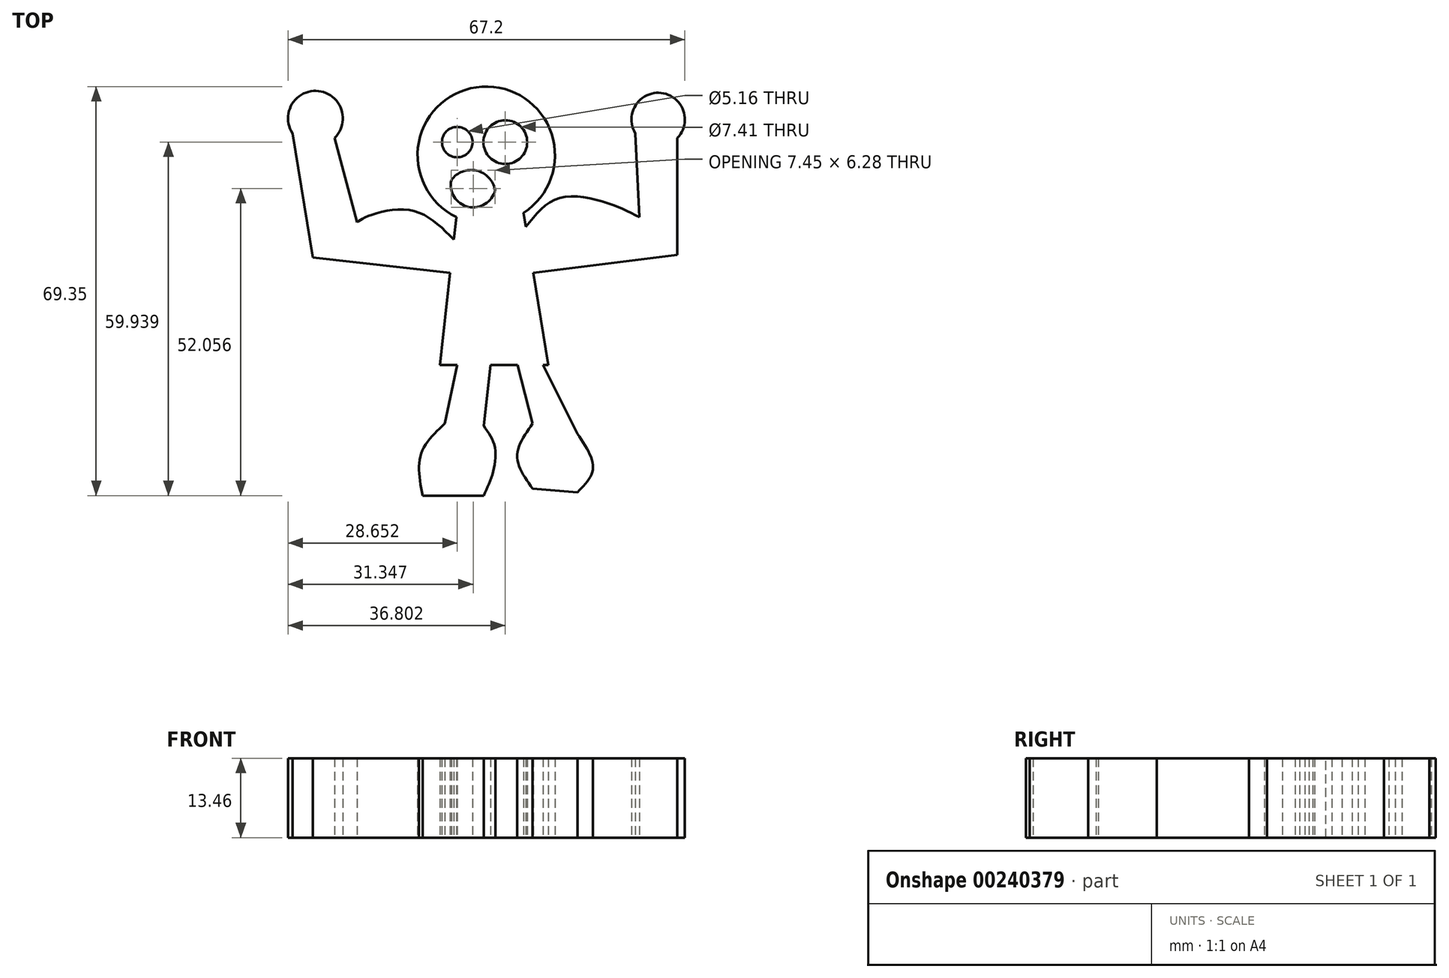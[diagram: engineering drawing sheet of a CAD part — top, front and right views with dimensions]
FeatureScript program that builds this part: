
annotation { "Feature Type Name" : "Feature", "Feature Type Description" : "" }
export const myFeature = defineFeature(function(context is Context, id is Id, definition is map)
    precondition{}
    {
        {
            var Q0;
            Q0=qCreatedBy(makeId("Top.planeOp"),FACE);
            var sketch = newSketch(context, id + "F0", { "sketchPlane" : qUnion([Q0])});
            skArc(sketch, "E0", {"start": v(-1.56, 31.76) * mm, "mid": v(-8.59, 53.15) * mm, "end": v(-12.93, 31.05) * mm});
            skLineSegment(sketch, "E1", {"start": v(-12.93, 31.05) * mm, "end": v(-13.35, 27.25) * mm});
            skLineSegment(sketch, "E2", {"start": v(-15.74, 5.98) * mm, "end": v(-12.8, 5.98) * mm});
            skLineSegment(sketch, "E3", {"start": v(2.62, 5.98) * mm, "end": v(0.1, 21.58) * mm});
            skFitSpline(sketch, "E4", {"points": [v(-1.17, 29.39) * mm, v(4.37, 34.25) * mm, v(12.82, 33.37) * mm, v(18.07, 31.04) * mm], "startDerivative": vector(14.2, 18.34) * mm, "endDerivative": vector(15.76, -8.07) * mm});
            skLineSegment(sketch, "E5", {"start": v(0, 21.57) * mm, "end": v(24.48, 24.63) * mm});
            skPoint(sketch, "E5.startSnap0", {"position": v(-14, 21.57) * mm});
            skLineSegment(sketch, "E6", {"start": v(24.48, 24.63) * mm, "end": v(24.48, 44.45) * mm});
            skLineSegment(sketch, "E7", {"start": v(17.38, 45.25) * mm, "end": v(18.07, 31.04) * mm});
            skLineSegment(sketch, "E8", {"start": v(-14, 21.57) * mm, "end": v(-37.26, 24.18) * mm});
            skLineSegment(sketch, "E9", {"start": v(-37.26, 24.18) * mm, "end": v(-40.68, 45.25) * mm});
            skFitSpline(sketch, "E10", {"points": [v(-13.35, 27.25) * mm, v(-20.7, 32.2) * mm, v(-28.27, 31.04) * mm, v(-29.73, 30.17) * mm], "startDerivative": vector(-15.75, 15.73) * mm, "endDerivative": vector(-5.81, -4.42) * mm});
            skLineSegment(sketch, "E11", {"start": v(-33.58, 44.45) * mm, "end": v(-29.73, 30.17) * mm});
            skLineSegment(sketch, "E12", {"start": v(-12.8, 5.98) * mm, "end": v(-14.87, -3.93) * mm});
            skLineSegment(sketch, "E13", {"start": v(-7.16, 5.98) * mm, "end": v(-8.32, -4.34) * mm});
            skLineSegment(sketch, "E14", {"start": v(-2.59, 5.98) * mm, "end": v(0, -3.93) * mm});
            skLineSegment(sketch, "E15", {"start": v(1.75, 5.98) * mm, "end": v(7.58, -5.68) * mm});
            skFitSpline(sketch, "E16", {"points": [v(-14.87, -3.93) * mm, v(-18.95, -9.18) * mm, v(-18.65, -16.18) * mm], "startDerivative": vector(-10.45, -9.85) * mm, "endDerivative": vector(2.82, -14.62) * mm});
            skLineSegment(sketch, "E17", {"start": v(-18.65, -16.18) * mm, "end": v(-8.32, -16.18) * mm});
            skFitSpline(sketch, "E18", {"points": [v(0, -3.93) * mm, v(-2.62, -9.47) * mm, v(0, -15.01) * mm], "startDerivative": vector(-7.87, -11.08) * mm, "endDerivative": vector(7.87, -11.08) * mm});
            skFitSpline(sketch, "E19", {"points": [v(7.58, -5.68) * mm, v(10.2, -11.51) * mm, v(7.58, -15.6) * mm], "startDerivative": vector(7.73, -11.48) * mm, "endDerivative": vector(-8.09, -8.27) * mm});
            skLineSegment(sketch, "E20", {"start": v(7.58, -15.6) * mm, "end": v(0, -15.01) * mm});
            skPoint(sketch, "E21.orphan", {"position": v(-12.24, 37.16) * mm});
            skLineSegment(sketch, "E22.trimOffspring", {"start": v(-1.17, 29.39) * mm, "end": v(-1.56, 31.76) * mm});
            skLineSegment(sketch, "E23.trimOffspring", {"start": v(-14, 21.57) * mm, "end": v(-15.74, 5.98) * mm});
            skPoint(sketch, "E24.orphan", {"position": v(-11.95, 10.06) * mm});
            skPoint(sketch, "E25.orphan", {"position": v(-6.7, 10.06) * mm});
            skPoint(sketch, "E26.orphan", {"position": v(-3.5, 9.47) * mm});
            skPoint(sketch, "E27.orphan", {"position": v(0, 9.47) * mm});
            skLineSegment(sketch, "E28.trimOffspring", {"start": v(-7.16, 5.98) * mm, "end": v(-2.59, 5.98) * mm});
            skLineSegment(sketch, "E29.trimOffspring", {"start": v(1.75, 5.98) * mm, "end": v(2.62, 5.98) * mm});
            skFitSpline(sketch, "E30", {"points": [v(-8.32, -4.34) * mm, v(-6.47, -7.67) * mm, v(-6.72, -12.2) * mm, v(-8.32, -16.18) * mm], "startDerivative": vector(7.23, -9.76) * mm, "endDerivative": vector(-5.36, -11.3) * mm});
            skArc(sketch, "E31", {"start": v(-33.58, 44.45) * mm, "mid": v(-36.28, 52.4) * mm, "end": v(-40.68, 45.25) * mm});
            skArc(sketch, "E32", {"start": v(24.48, 44.45) * mm, "mid": v(21.75, 52.09) * mm, "end": v(17.38, 45.25) * mm});
            skSolve(sketch);
        }
        {
            var Q0;
            Q0 = qSketchRegion(id + "F0", true);
            extrude(context, id + "F1", {"entities" : qUnion([Q0]), "depth" : 13.46 * mm});
        }
        {
            var Q0;
            Q0=qCreatedBy(makeId("Top.planeOp"),FACE);
            var sketch = newSketch(context, id + "F2", { "sketchPlane" : qUnion([Q0])});
            skCircle(sketch, "E33", {"center": v(-12.79, 43.76) * mm, "radius": 2.58 * mm});
            skCircle(sketch, "E34", {"center": v(-4.64, 43.76) * mm, "radius": 3.7 * mm});
            skArc(sketch, "E35", {"start": v(-13.78, 37.34) * mm, "mid": v(-10.93, 32.79) * mm, "end": v(-6.37, 35.6) * mm});
            skArc(sketch, "E36", {"start": v(-6.37, 35.6) * mm, "mid": v(-9.5, 38.92) * mm, "end": v(-13.78, 37.34) * mm});
            skSolve(sketch);
        }
        {
            var Q0;
            Q0 = qSketchRegion(id + "F2", true);
            extrude(context, id + "F3", {"entities" : qUnion([Q0]), "operationType" : NewBodyOperationType.REMOVE, "depth" : 51.05 * mm});
        }
    });
